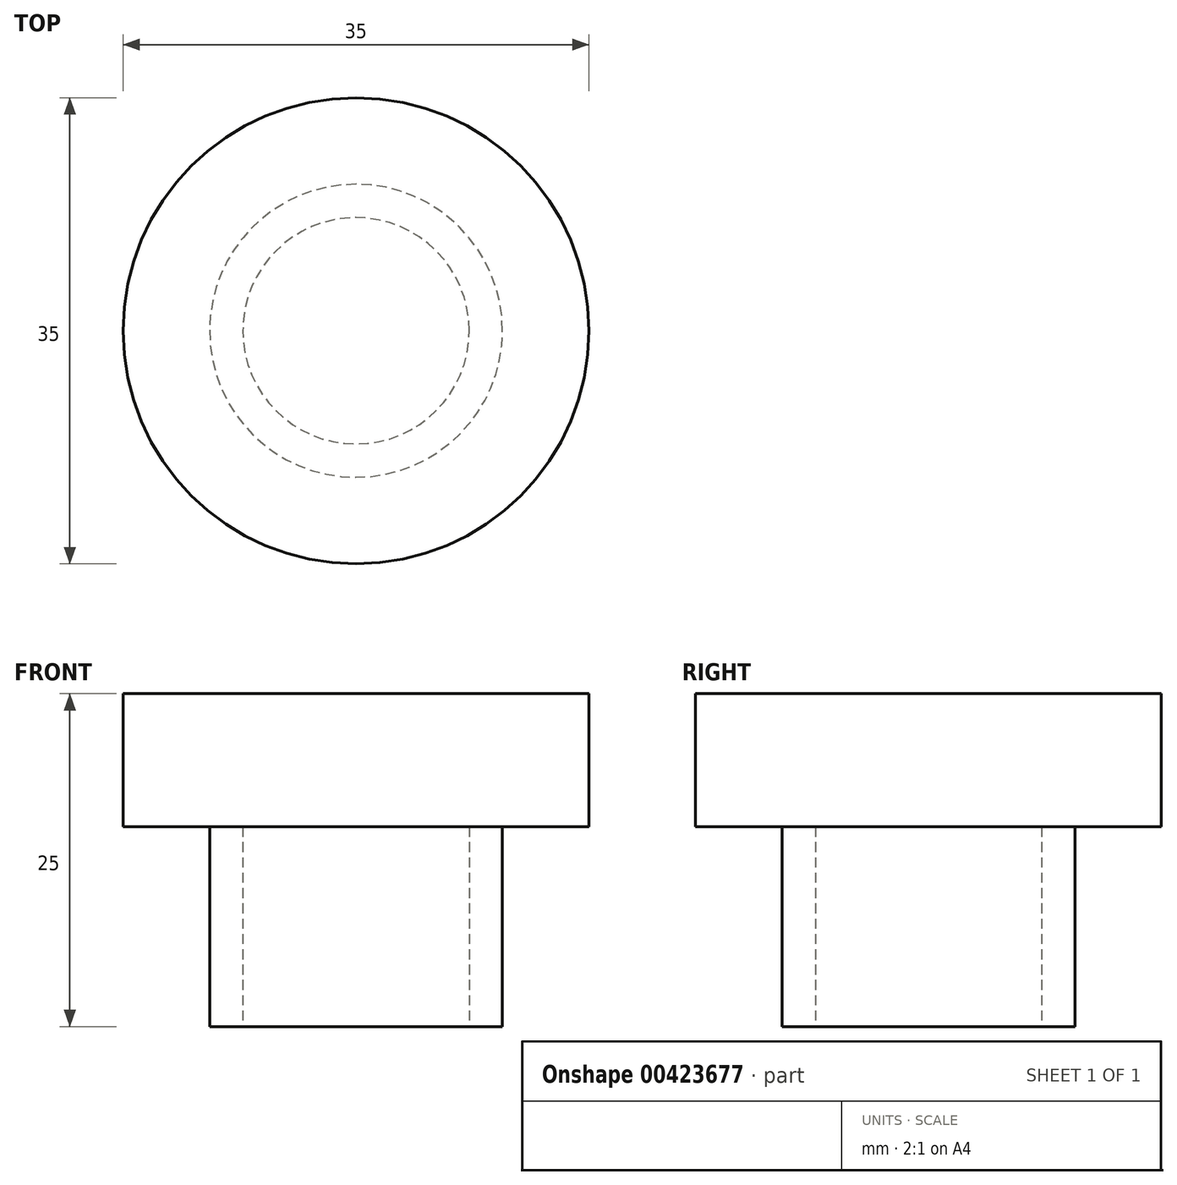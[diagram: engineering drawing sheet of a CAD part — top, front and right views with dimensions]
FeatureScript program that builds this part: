
annotation { "Feature Type Name" : "Feature", "Feature Type Description" : "" }
export const myFeature = defineFeature(function(context is Context, id is Id, definition is map)
    precondition{}
    {
        {
            var Q0;
            Q0=qCreatedBy(makeId("Top.planeOp"),FACE);
            var sketch = newSketch(context, id + "F0", { "sketchPlane" : qUnion([Q0])});
            skCircle(sketch, "E0", {"center": v(0, 0) * mm, "radius": 8.5 * mm});
            skCircle(sketch, "E1", {"center": v(0, 0) * mm, "radius": 11 * mm});
            skSolve(sketch);
        }
        {
            var Q0;
            Q0=makeQuery(id+"F0.imprint","IMPRINT",FACE,{"disambiguationData":[TD([[makeQuery(id+"F0.imprint","IMPRINT",EDGE,{"derivedFrom":sQuery(id+"F0.wireOp",EDGE,"E0")}),-1.0]])]});
            var Q1;
            Q1=sQuery(id+"F0.wireOp",EDGE,"E1");
            var Q2;
            Q2=sQuery(id+"F0.wireOp",EDGE,"E0");
            extrude(context, id + "F1", {"entities" : qUnion([Q0]), "surfaceEntities" : qUnion([Q1, Q2]), "depth" : 15 * mm});
        }
        {
            var Q0;
            Q0=makeQuery(id+"F1.opExtrude","CAP_FACE",FACE,{"disambiguationData":[OSD([sQuery(id+"F0.wireOp",EDGE,"E0"),sQuery(id+"F0.wireOp",EDGE,"E1")])],"isStart":false});
            var sketch = newSketch(context, id + "F2", { "sketchPlane" : qUnion([Q0])});
            skCircle(sketch, "E2", {"center": v(0, 0) * mm, "radius": 17.5 * mm});
            skSolve(sketch);
        }
        {
            var Q0;
            Q0=qSketchRegion(id+"F2",true);
            extrude(context, id + "F3", {"entities" : qUnion([Q0]), "operationType" : NewBodyOperationType.ADD, "depth" : 10 * mm});
        }
    });
